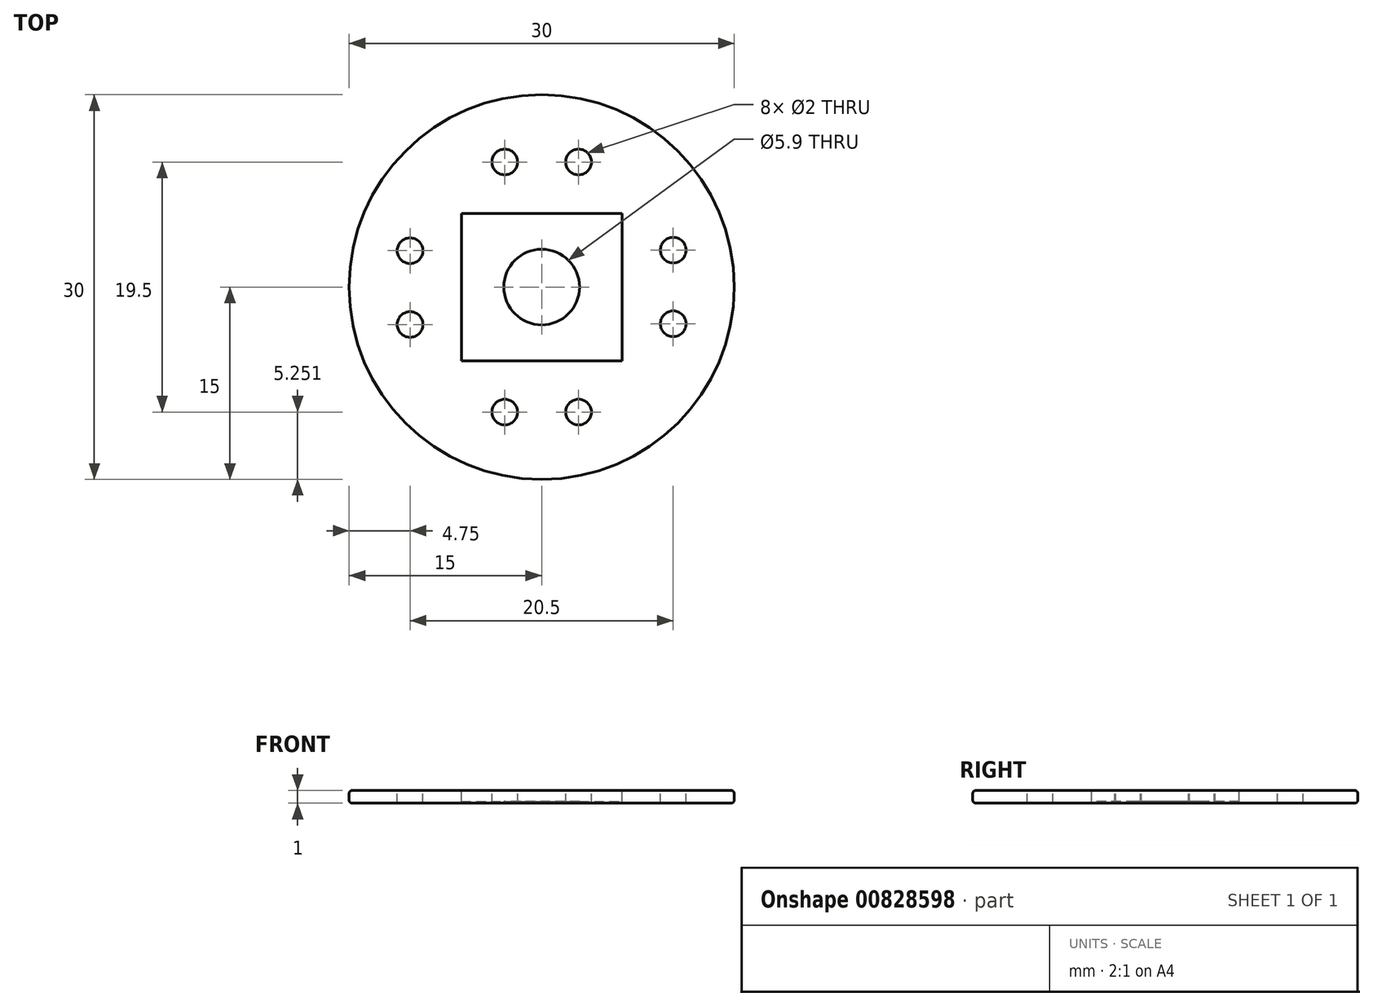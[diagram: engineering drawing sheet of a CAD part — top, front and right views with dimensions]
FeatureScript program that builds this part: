
annotation { "Feature Type Name" : "Feature", "Feature Type Description" : "" }
export const myFeature = defineFeature(function(context is Context, id is Id, definition is map)
    precondition{}
    {
        {
            var Q0;
            Q0=qCreatedBy(makeId("Top.planeOp"),FACE);
            var sketch = newSketch(context, id + "F0", { "sketchPlane" : qUnion([Q0])});
            skCircle(sketch, "E0", {"center": v(0, 0) * mm, "radius": 15 * mm});
            skSolve(sketch);
        }
        {
            var Q0;
            Q0=makeQuery(id+"F0.imprint","IMPRINT",FACE,{"disambiguationData":[TD([[makeQuery(id+"F0.imprint","IMPRINT",EDGE,{"derivedFrom":sQuery(id+"F0.wireOp",EDGE,"E0")}),1.0]])]});
            extrude(context, id + "F1", {"entities" : qUnion([Q0]), "depth" : 1 * mm, "offsetDistance" : 25 * mm});
        }
        {
            var Q0;
            Q0=makeQuery(id+"F1.opExtrude","CAP_FACE",FACE,{"disambiguationData":[OSD([sQuery(id+"F0.wireOp",EDGE,"E0")])],"isStart":false});
            var sketch = newSketch(context, id + "F2", { "sketchPlane" : qUnion([Q0])});
            skLineSegment(sketch, "E1.bottom", {"start": v(-6.25, 5.75) * mm, "end": v(6.25, 5.75) * mm});
            skLineSegment(sketch, "E1.top", {"start": v(-6.25, -5.75) * mm, "end": v(6.25, -5.75) * mm});
            skLineSegment(sketch, "E1.left", {"start": v(-6.25, 5.75) * mm, "end": v(-6.25, -5.75) * mm});
            skLineSegment(sketch, "E1.right", {"start": v(6.25, 5.75) * mm, "end": v(6.25, -5.75) * mm});
            skSolve(sketch);
        }
        {
            var Q0;
            Q0=makeQuery(id+"F2.imprint","IMPRINT",FACE,{"disambiguationData":[TD([[makeQuery(id+"F2.imprint","IMPRINT",EDGE,{"derivedFrom":sQuery(id+"F2.wireOp",EDGE,"E1.bottom")}),-1.0]])]});
            extrude(context, id + "F3", {"entities" : qUnion([Q0]), "operationType" : NewBodyOperationType.REMOVE, "oppositeDirection" : true, "depth" : 0.85 * mm, "offsetDistance" : 25 * mm});
        }
        {
            var Q0;
            Q0=qCreatedBy(makeId("Top.planeOp"),FACE);
            cPlane(context, id + "F4", {"entities" : qUnion([Q0]), "cplaneType" : CPlaneType.OFFSET, "offset" : 0.15 * mm, "width" : 150 * mm, "height" : 150 * mm});
        }
        {
            var Q0;
            Q0=qCreatedBy(id+"F4.planeOp",FACE);
            var sketch = newSketch(context, id + "F5", { "sketchPlane" : qUnion([Q0])});
            skCircle(sketch, "E2", {"center": v(0, 0) * mm, "radius": 2.95 * mm});
            skSolve(sketch);
        }
        {
            var Q0;
            Q0 = qSketchRegion(id + "F5", true);
            extrude(context, id + "F6", {"entities" : qUnion([Q0]), "operationType" : NewBodyOperationType.REMOVE, "oppositeDirection" : true, "depth" : 0.15 * mm, "offsetDistance" : 25 * mm});
        }
        {
            var Q0;
            Q0=makeQuery(id+"F1.opExtrude","CAP_EDGE",EDGE,{"disambiguationData":[OSD([sQuery(id+"F0.wireOp",EDGE,"E0")])],"isStart":false});
            var Q1;
            Q1=makeQuery(id+"F1.opExtrude","CAP_EDGE",EDGE,{"disambiguationData":[OSD([sQuery(id+"F0.wireOp",EDGE,"E0")])],"isStart":true});
            var Q2;
            Q2=makeQuery(id+"F1.opExtrude","CAP_EDGE",EDGE,{"disambiguationData":[OSD([sQuery(id+"F0.wireOp",EDGE,"E0")])],"isStart":false});
            fillet(context, id + "F7", {"entities" : qUnion([Q0, Q1, Q2]), "radius" : 0.25 * mm, "tangentPropagation" : true, "allowEdgeOverflow" : false});
        }
        {
            var Q0;
            Q0=makeQuery(id+"F1.opExtrude","CAP_FACE",FACE,{"disambiguationData":[OSD([sQuery(id+"F0.wireOp",EDGE,"E0")])],"isStart":false});
            var sketch = newSketch(context, id + "F8", { "sketchPlane" : qUnion([Q0])});
            skCircle(sketch, "E3", {"center": v(-10.25, 2.83) * mm, "radius": 1 * mm});
            skCircle(sketch, "E4", {"center": v(-10.25, -2.92) * mm, "radius": 1 * mm});
            skLineSegment(sketch, "E5", {"start": v(-2.88, 13.32) * mm, "end": v(-2.87, -11.69) * mm, "construction": true});
            skLineSegment(sketch, "E6", {"start": v(2.87, 13.36) * mm, "end": v(2.88, -11.51) * mm, "construction": true});
            skCircle(sketch, "E7", {"center": v(-2.87, -9.75) * mm, "radius": 1 * mm});
            skCircle(sketch, "E8", {"center": v(2.88, -9.75) * mm, "radius": 1 * mm});
            skLineSegment(sketch, "E9", {"start": v(-17, 2.87) * mm, "end": v(17.76, 2.88) * mm, "construction": true});
            skLineSegment(sketch, "E10", {"start": v(17.76, -2.83) * mm, "end": v(-17.34, -2.92) * mm, "construction": true});
            skCircle(sketch, "E11", {"center": v(10.25, 2.88) * mm, "radius": 1 * mm});
            skCircle(sketch, "E12", {"center": v(10.25, -2.86) * mm, "radius": 1 * mm});
            skCircle(sketch, "E13", {"center": v(-2.88, 9.75) * mm, "radius": 1 * mm});
            skCircle(sketch, "E14", {"center": v(2.87, 9.75) * mm, "radius": 1 * mm});
            skSolve(sketch);
        }
        {
            var Q0;
            Q0=makeQuery(id+"F8.imprint","IMPRINT",FACE,{"disambiguationData":[TD([[makeQuery(id+"F8.imprint","IMPRINT",EDGE,{"derivedFrom":sQuery(id+"F8.wireOp",EDGE,"E3")}),1.0]])]});
            var Q1;
            Q1=makeQuery(id+"F8.imprint","IMPRINT",FACE,{"disambiguationData":[TD([[makeQuery(id+"F8.imprint","IMPRINT",EDGE,{"derivedFrom":sQuery(id+"F8.wireOp",EDGE,"E4")}),1.0]])]});
            var Q2;
            Q2=makeQuery(id+"F8.imprint","IMPRINT",FACE,{"disambiguationData":[TD([[makeQuery(id+"F8.imprint","IMPRINT",EDGE,{"derivedFrom":sQuery(id+"F8.wireOp",EDGE,"E13")}),1.0]])]});
            var Q3;
            Q3=makeQuery(id+"F8.imprint","IMPRINT",FACE,{"disambiguationData":[TD([[makeQuery(id+"F8.imprint","IMPRINT",EDGE,{"derivedFrom":sQuery(id+"F8.wireOp",EDGE,"E14")}),1.0]])]});
            var Q4;
            Q4=makeQuery(id+"F8.imprint","IMPRINT",FACE,{"disambiguationData":[TD([[makeQuery(id+"F8.imprint","IMPRINT",EDGE,{"derivedFrom":sQuery(id+"F8.wireOp",EDGE,"E11")}),1.0]])]});
            var Q5;
            Q5=makeQuery(id+"F8.imprint","IMPRINT",FACE,{"disambiguationData":[TD([[makeQuery(id+"F8.imprint","IMPRINT",EDGE,{"derivedFrom":sQuery(id+"F8.wireOp",EDGE,"E12")}),1.0]])]});
            var Q6;
            Q6=makeQuery(id+"F8.imprint","IMPRINT",FACE,{"disambiguationData":[TD([[makeQuery(id+"F8.imprint","IMPRINT",EDGE,{"derivedFrom":sQuery(id+"F8.wireOp",EDGE,"E8")}),1.0]])]});
            var Q7;
            Q7=makeQuery(id+"F8.imprint","IMPRINT",FACE,{"disambiguationData":[TD([[makeQuery(id+"F8.imprint","IMPRINT",EDGE,{"derivedFrom":sQuery(id+"F8.wireOp",EDGE,"E7")}),1.0]])]});
            var Q8;
            Q8=sQuery(id+"F8.wireOp",EDGE,"E12");
            var Q9;
            Q9=sQuery(id+"F8.wireOp",EDGE,"E8");
            var Q10;
            Q10=sQuery(id+"F8.wireOp",EDGE,"E7");
            var Q11;
            Q11=sQuery(id+"F8.wireOp",EDGE,"E4");
            var Q12;
            Q12=sQuery(id+"F8.wireOp",EDGE,"E3");
            var Q13;
            Q13=sQuery(id+"F8.wireOp",EDGE,"E13");
            var Q14;
            Q14=sQuery(id+"F8.wireOp",EDGE,"E14");
            var Q15;
            Q15=sQuery(id+"F8.wireOp",EDGE,"E11");
            var Q16;
            Q16=makeQuery(id+"F1.opExtrude","SWEPT_BODY",BODY,{"disambiguationData":[OSD([sQuery(id+"F0.wireOp",EDGE,"E0")])]});
            extrude(context, id + "F9", {"entities" : qUnion([Q0, Q1, Q2, Q3, Q4, Q5, Q6, Q7]), "operationType" : NewBodyOperationType.REMOVE, "surfaceEntities" : qUnion([Q8, Q9, Q10, Q11, Q12, Q13, Q14, Q15]), "oppositeDirection" : true, "depth" : 1 * mm, "endBoundEntityBody" : qUnion([Q16]), "offsetDistance" : 25 * mm});
        }
    });
